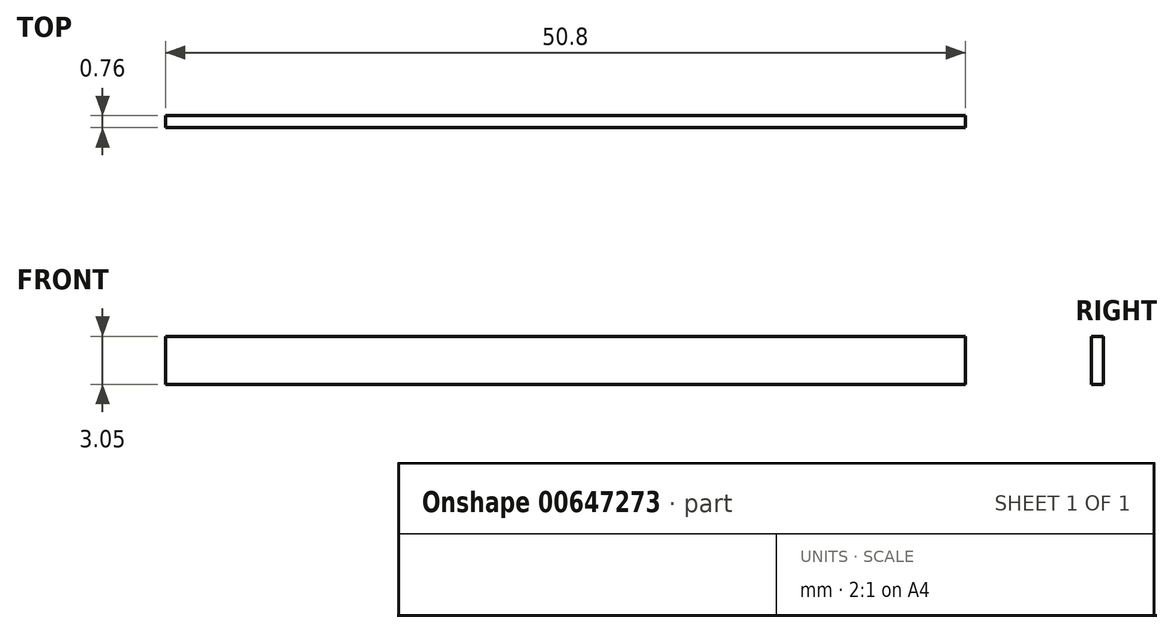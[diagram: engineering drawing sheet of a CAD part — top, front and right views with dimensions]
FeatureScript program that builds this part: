
annotation { "Feature Type Name" : "Feature", "Feature Type Description" : "" }
export const myFeature = defineFeature(function(context is Context, id is Id, definition is map)
    precondition{}
    {
        {
            var Q0;
            Q0=qCreatedBy(makeId("Top.planeOp"),FACE);
            var sketch = newSketch(context, id + "F0", { "sketchPlane" : qUnion([Q0])});
            skLineSegment(sketch, "E0", {"start": v(0, 0) * mm, "end": v(50.8, 0) * mm});
            skLineSegment(sketch, "E1", {"start": v(50.8, 0) * mm, "end": v(50.8, 0.76) * mm});
            skLineSegment(sketch, "E2", {"start": v(50.8, 0.76) * mm, "end": v(0, 0.76) * mm});
            skLineSegment(sketch, "E3", {"start": v(0, 0.76) * mm, "end": v(0, 0) * mm});
            skLineSegment(sketch, "E4", {"start": v(50.8, 0.76) * mm, "end": v(50.3, 2.03) * mm});
            skLineSegment(sketch, "E5", {"start": v(50.3, 2.03) * mm, "end": v(50.3, 2.03) * mm});
            skLineSegment(sketch, "E6", {"start": v(50.3, 2.03) * mm, "end": v(49.8, 0.76) * mm});
            skLineSegment(sketch, "E7", {"start": v(50.3, 2.03) * mm, "end": v(50.3, 0.76) * mm});
            skLineSegment(sketch, "E8", {"start": v(49.8, 0.76) * mm, "end": v(50.8, 0.76) * mm});
            skLineSegment(sketch, "E9.1.0.0", {"start": v(49.8, 0.76) * mm, "end": v(49.31, 2.03) * mm});
            skLineSegment(sketch, "E9.1.0.1", {"start": v(49.3, 2.03) * mm, "end": v(48.8, 0.76) * mm});
            skLineSegment(sketch, "E9.1.0.2", {"start": v(48.8, 0.76) * mm, "end": v(49.8, 0.76) * mm});
            skLineSegment(sketch, "E9.2.0.0", {"start": v(48.8, 0.76) * mm, "end": v(48.32, 2.03) * mm});
            skLineSegment(sketch, "E9.2.0.1", {"start": v(48.3, 2.03) * mm, "end": v(47.8, 0.76) * mm});
            skLineSegment(sketch, "E9.2.0.2", {"start": v(47.8, 0.76) * mm, "end": v(48.8, 0.76) * mm});
            skLineSegment(sketch, "E9.direction1", {"start": v(50.8, 0.76) * mm, "end": v(49.8, 0.76) * mm, "construction": true});
            skSolve(sketch);
        }
        {
            var Q0;
            Q0=makeQuery(id+"F0.imprint","IMPRINT",FACE,{"disambiguationData":[TD([[makeQuery(id+"F0.imprint","IMPRINT",EDGE,{"derivedFrom":sQuery(id+"F0.wireOp",EDGE,"E0")}),1.0]])]});
            extrude(context, id + "F1", {"entities" : qUnion([Q0]), "depth" : 3.05 * mm, "offsetDistance" : 25.4 * mm});
        }
    });
